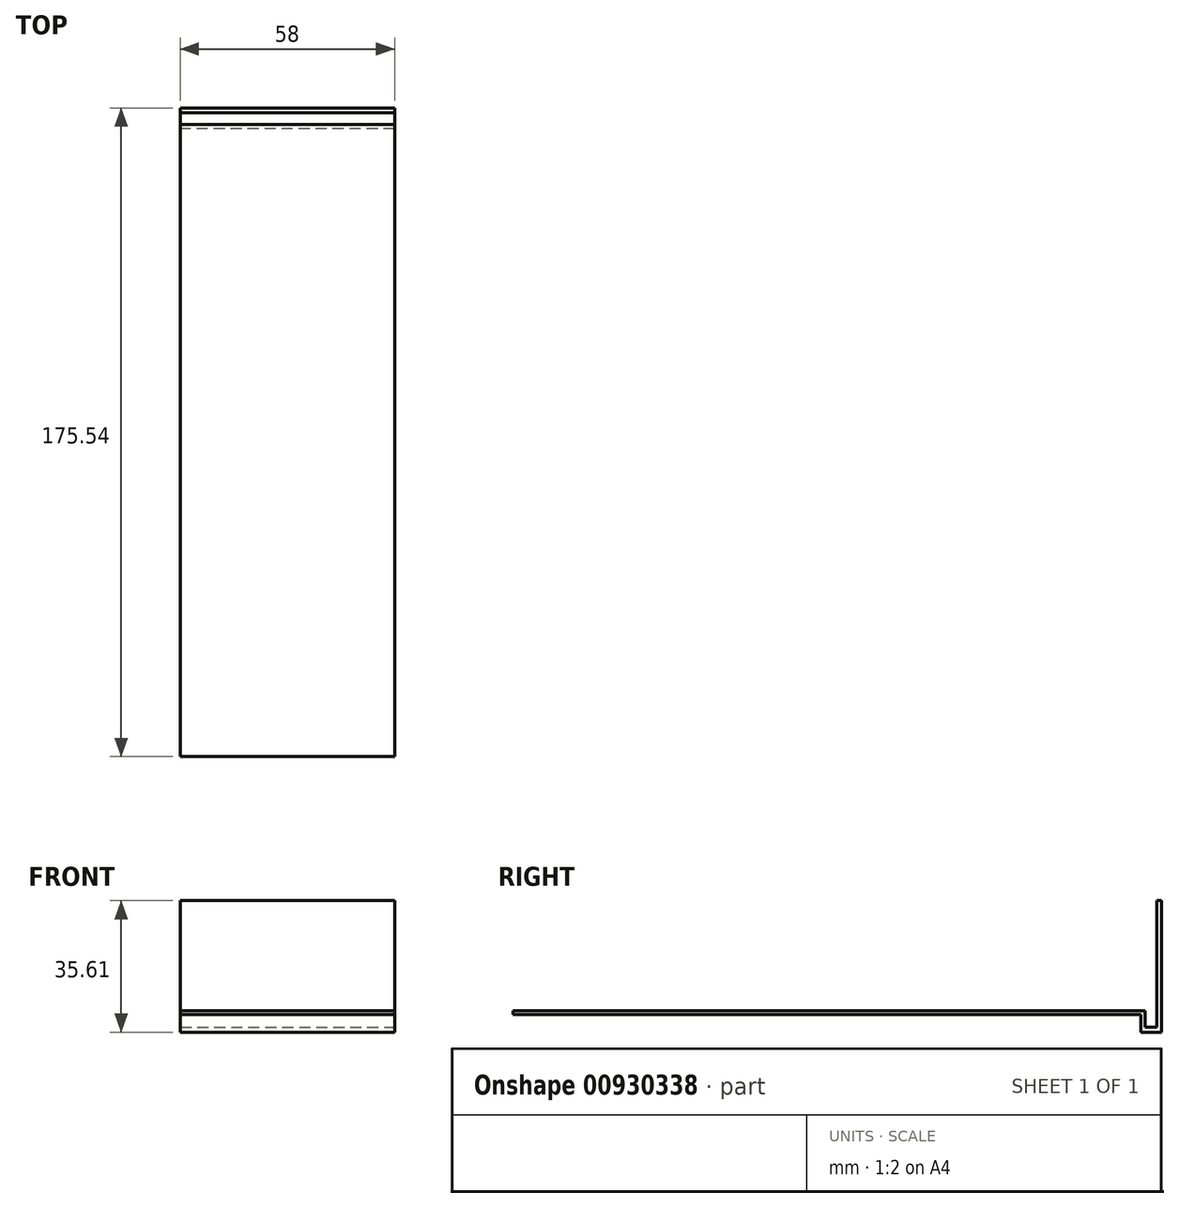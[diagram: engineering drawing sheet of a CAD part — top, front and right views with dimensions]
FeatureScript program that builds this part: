
annotation { "Feature Type Name" : "Feature", "Feature Type Description" : "" }
export const myFeature = defineFeature(function(context is Context, id is Id, definition is map)
    precondition{}
    {
        {
            var Q0;
            Q0=qCreatedBy(makeId("Top.planeOp"),FACE);
            var sketch = newSketch(context, id + "F0", { "sketchPlane" : qUnion([Q0])});
            skLineSegment(sketch, "E0.bottom", {"start": v(29, 85) * mm, "end": v(-29, 85) * mm});
            skLineSegment(sketch, "E0.top", {"start": v(29, -85) * mm, "end": v(-29, -85) * mm});
            skLineSegment(sketch, "E0.left", {"start": v(29, 85) * mm, "end": v(29, -85) * mm});
            skLineSegment(sketch, "E0.right", {"start": v(-29, 85) * mm, "end": v(-29, -85) * mm});
            skPoint(sketch, "E0.middle", {"position": v(0, 0) * mm});
            skSolve(sketch);
        }
        {
            var Q0;
            Q0=makeQuery(id+"F0.imprint","IMPRINT",FACE,{"disambiguationData":[TD([[makeQuery(id+"F0.imprint","IMPRINT",EDGE,{"derivedFrom":sQuery(id+"F0.wireOp",EDGE,"E0.bottom")}),1.0]])]});
            extrude(context, id + "F1", {"entities" : qUnion([Q0]), "depth" : 1 * mm, "offsetDistance" : 25 * mm});
        }
        {
            var Q0;
            Q0=makeQuery(id+"F1.opExtrude","SWEPT_FACE",FACE,{"disambiguationData":[OSD([sQuery(id+"F0.wireOp",EDGE,"E0.left")])]});
            var sketch = newSketch(context, id + "F2", { "sketchPlane" : qUnion([Q0])});
            skLineSegment(sketch, "E1.bottom", {"start": v(85, 1) * mm, "end": v(86.1, 1) * mm});
            skLineSegment(sketch, "E1.top", {"start": v(85, -4.8) * mm, "end": v(86.1, -4.8) * mm});
            skLineSegment(sketch, "E1.left", {"start": v(85, 1) * mm, "end": v(85, -4.8) * mm});
            skLineSegment(sketch, "E1.right", {"start": v(86.1, 1) * mm, "end": v(86.1, -3.46) * mm});
            skLineSegment(sketch, "E2.bottom", {"start": v(86.1, -4.8) * mm, "end": v(90.54, -4.8) * mm});
            skLineSegment(sketch, "E2.top", {"start": v(86.1, -3.46) * mm, "end": v(89.3, -3.46) * mm});
            skLineSegment(sketch, "E2.right", {"start": v(90.54, -4.8) * mm, "end": v(90.54, -3.46) * mm});
            skLineSegment(sketch, "E3.top", {"start": v(90.54, 30.8) * mm, "end": v(89.3, 30.8) * mm});
            skLineSegment(sketch, "E3.left", {"start": v(90.54, -3.46) * mm, "end": v(90.54, 30.8) * mm});
            skLineSegment(sketch, "E3.right", {"start": v(89.3, -3.46) * mm, "end": v(89.3, 30.8) * mm});
            skSolve(sketch);
        }
        {
            var Q0;
            Q0 = qSketchRegion(id + "F2", true);
            var Q1;
            Q1=makeQuery(id+"F1.opExtrude","SWEPT_FACE",FACE,{"disambiguationData":[OSD([sQuery(id+"F0.wireOp",EDGE,"E0.right")])]});
            extrude(context, id + "F3", {"entities" : qUnion([Q0]), "operationType" : NewBodyOperationType.ADD, "endBound" : BoundingType.UP_TO_SURFACE, "oppositeDirection" : true, "depth" : 25 * mm, "endBoundEntityFace" : qUnion([Q1]), "offsetDistance" : 25 * mm});
        }
    });
